# Revit family: DLH-Series Bar Joist-Section
name_source: partatom
category: Detail Items
revit_build: Autodesk Revit Architecture 2012 (Build: 20110210_1515)
units: mm (PartAtom-declared; Revit-internal decimal feet)

## types (42) — shared parameters

## per-type parameters (varying)
| type | Depth | Keynote | Wt |
| 52DLH10 | 52" | 05 21 00.D1 | 25 |
| 52DLH11 | 52" | 05 21 00.D2 | 26 |
| 52DLH12 | 52" | 05 21 00.D3 | 29 |
| 52DLH13 | 52" | 05 21 00.D4 | 34 |
| 52DLH14 | 52" | 05 21 00.D5 | 39 |
| 52DLH15 | 52" | 05 21 00.D6 | 42 |
| 52DLH16 | 52" | 05 21 00.D7 | 45 |
| 52DLH17 | 52" | 05 21 00.D8 | 52 |
| 56DLH11 | 56" | 05 21 00.D9 | 26 |
| 56DLH12 | 56" | 05 21 00.D10 | 30 |
| 56DLH13 | 56" | 05 21 00.D11 | 34 |
| 56DLH14 | 56" | 05 21 00.D12 | 39 |
| 56DLH15 | 56" | 05 21 00.D13 | 42 |
| 56DLH16 | 56" | 05 21 00.D14 | 46 |
| 56DLH17 | 56" | 05 21 00.D15 | 51 |
| 60DLH12 | 60" | 05 21 00.D16 | 29 |
| 60DLH13 | 60" | 05 21 00.D17 | 35 |
| 60DLH14 | 60" | 05 21 00.D18 | 40 |
| 60DLH15 | 60" | 05 21 00.D19 | 43 |
| 60DLH16 | 60" | 05 21 00.D20 | 46 |
| 60DLH17 | 60" | 05 21 00.D21 | 52 |
| 60DLH18 | 60" | 05 21 00.D22 | 59 |
| 64DLH12 | 64" | 05 21 00.D23 | 31 |
| 64DLH13 | 64" | 05 21 00.D24 | 34 |
| 64DLH14 | 64" | 05 21 00.D25 | 40 |
| 64DLH15 | 64" | 05 21 00.D26 | 43 |
| 64DLH16 | 64" | 05 21 00.D27 | 46 |
| 64DLH17 | 64" | 05 21 00.D28 | 52 |
| 64DLH18 | 64" | 05 21 00.D29 | 59 |
| 68DLH13 | 68" | 05 21 00.D30 | 37 |
| 68DLH14 | 68" | 05 21 00.D31 | 40 |
| 68DLH15 | 68" | 05 21 00.D32 | 44 |
| 68DLH16 | 68" | 05 21 00.D33 | 49 |
| 68DLH17 | 68" | 05 21 00.D34 | 55 |
| 68DLH18 | 68" | 05 21 00.D35 | 61 |
| 68DLH19 | 68" | 05 21 00.D36 | 67 |
| 72DLH14 | 72" | 05 21 00.D37 | 41 |
| 72DLH15 | 72" | 05 21 00.D38 | 44 |
| 72DLH16 | 72" | 05 21 00.D39 | 50 |
| 72DLH17 | 72" | 05 21 00.D40 | 56 |
| 72DLH18 | 72" | 05 21 00.D41 | 59 |
| 72DLH19 | 72" | 05 21 00.D42 | 70 |
